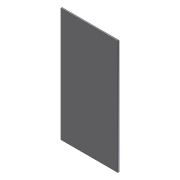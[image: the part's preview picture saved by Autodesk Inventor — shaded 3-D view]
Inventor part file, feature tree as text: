
AUTODESK INVENTOR PART (.ipt)
format: ipt  version: 2012 (Build 160160000, 160)  size: 64,000 bytes
history: native  units: in
note: dims shown in document units (in); Inventor stores cm internally (conversion verified against a paired STEP export)
features: extrude x1, sketch x1
ambient origin geometry x8: Origin, YZ Plane, XZ Plane, XY Plane, X Axis, Y Axis, Z Axis, Center Point
bodies: Solid1 (feature_tree)
feature tree (2):
  extrude  "Extrusion1"  Depth=48.0in
  sketch  "Sketch1"  dims[d0=24.0in d1=48.0in d2=0.5in d3=0.0in]
